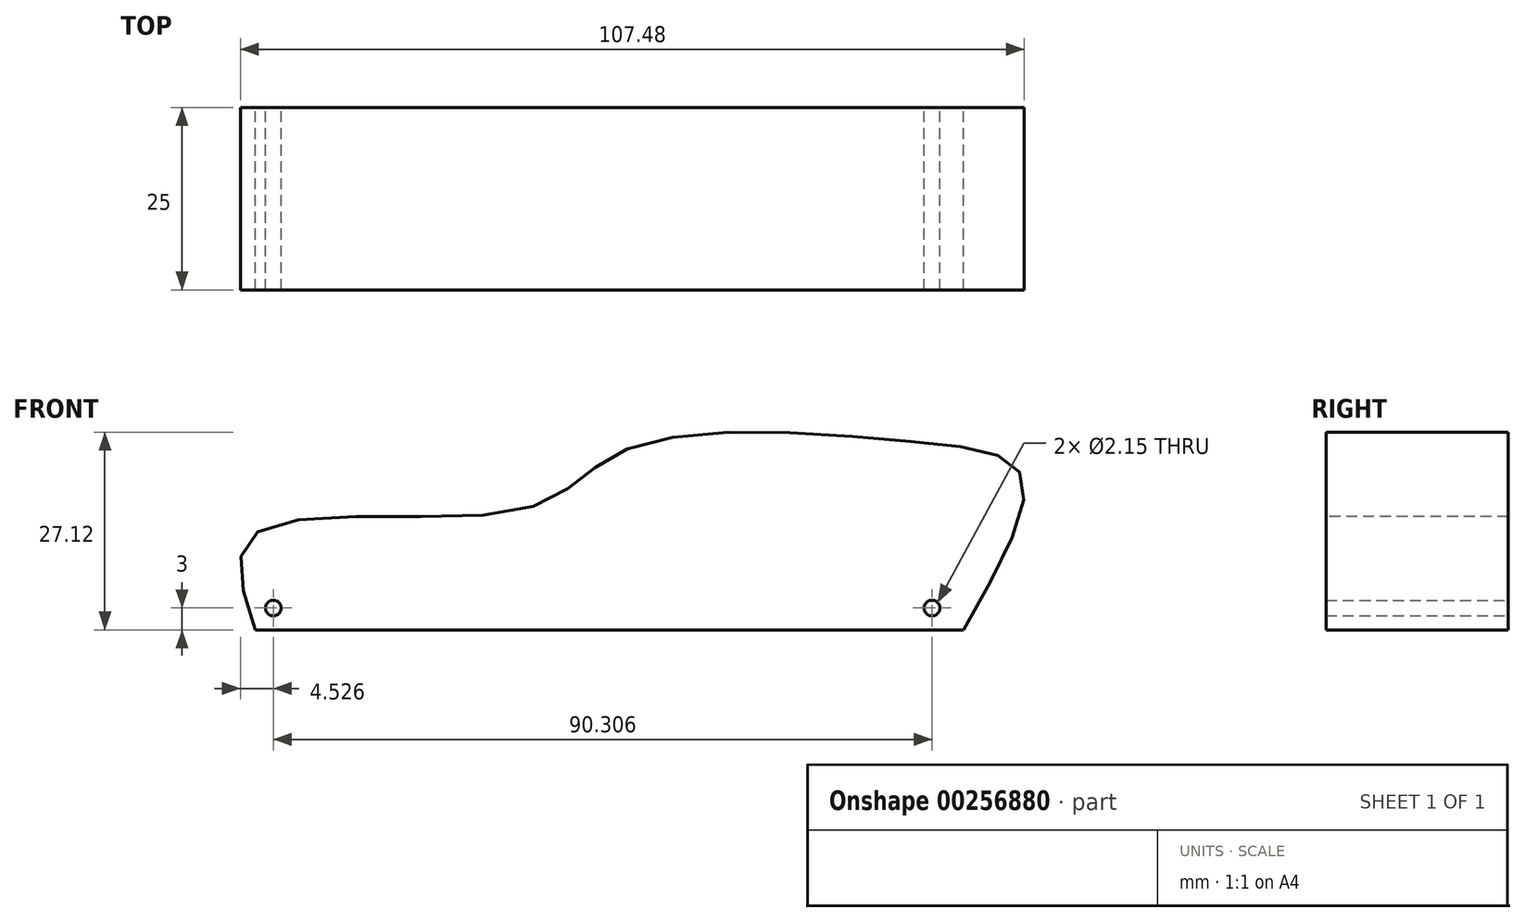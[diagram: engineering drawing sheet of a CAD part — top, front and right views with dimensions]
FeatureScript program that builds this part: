
annotation { "Feature Type Name" : "Feature", "Feature Type Description" : "" }
export const myFeature = defineFeature(function(context is Context, id is Id, definition is map)
    precondition{}
    {
        {
            var Q0;
            Q0=qCreatedBy(makeId("Front.planeOp"),FACE);
            var sketch = newSketch(context, id + "F0", { "sketchPlane" : qUnion([Q0])});
            skLineSegment(sketch, "E0", {"start": v(-46.22, 0) * mm, "end": v(0, 0) * mm});
            skLineSegment(sketch, "E1", {"start": v(0, 0) * mm, "end": v(50.9, 0) * mm});
            skFitSpline(sketch, "E2", {"points": [v(-46.22, 0) * mm, v(-46.22, 13.24) * mm, v(-9.51, 16.55) * mm, v(5.06, 24.94) * mm, v(43.9, 25.82) * mm, v(58.91, 20.97) * mm, v(50.9, 0) * mm], "startDerivative": vector(-42, 126.6) * mm, "endDerivative": vector(-87.27, -152.55) * mm});
            skLineSegment(sketch, "E3", {"start": v(-42.18, 0) * mm, "end": v(-42.18, 4.4) * mm});
            skSolve(sketch);
        }
        {
            var Q0;
            Q0=makeQuery(id+"F0.imprint","IMPRINT",FACE,{"disambiguationData":[TD([[makeQuery(id+"F0.imprint","IMPRINT",EDGE,{"derivedFrom":sQuery(id+"F0.wireOp",EDGE,"E0")}),1.0]])]});
            extrude(context, id + "F1", {"entities" : qUnion([Q0]), "depth" : 25 * mm});
        }
        {
            var Q0;
            Q0=makeQuery(id+"F1.opExtrude","CAP_FACE",FACE,{"disambiguationData":[OSD([sQuery(id+"F0.wireOp",EDGE,"E0"),sQuery(id+"F0.wireOp",EDGE,"E1"),sQuery(id+"F0.wireOp",EDGE,"E2")])],"isStart":false});
            var sketch = newSketch(context, id + "F2", { "sketchPlane" : qUnion([Q0])});
            skSolve(sketch);
        }
        {
            var Q0;
            Q0=makeQuery(id+"F1.opExtrude","CAP_FACE",FACE,{"disambiguationData":[OSD([sQuery(id+"F0.wireOp",EDGE,"E0"),sQuery(id+"F0.wireOp",EDGE,"E1"),sQuery(id+"F0.wireOp",EDGE,"E2")])],"isStart":true});
            var sketch = newSketch(context, id + "F3", { "sketchPlane" : qUnion([Q0])});
            skLineSegment(sketch, "E4", {"start": v(43.74, 3) * mm, "end": v(43.74, 0) * mm});
            skCircle(sketch, "E5", {"center": v(43.74, 3) * mm, "radius": 1.07 * mm});
            skLineSegment(sketch, "E6", {"start": v(-46.56, 0) * mm, "end": v(-46.56, 3) * mm});
            skCircle(sketch, "E7", {"center": v(-46.56, 3) * mm, "radius": 1.07 * mm});
            skSolve(sketch);
        }
        {
            var Q0;
            Q0=makeQuery(id+"F3.imprint","IMPRINT",FACE,{"disambiguationData":[TD([[makeQuery(id+"F3.imprint","IMPRINT",EDGE,{"derivedFrom":sQuery(id+"F3.wireOp",EDGE,"E7")}),1.0]])]});
            extrude(context, id + "F4", {"entities" : qUnion([Q0]), "operationType" : NewBodyOperationType.REMOVE, "endBound" : BoundingType.THROUGH_ALL, "oppositeDirection" : true, "depth" : 25 * mm});
        }
        {
            var Q0;
            Q0=makeQuery(id+"F3.imprint","IMPRINT",FACE,{"disambiguationData":[TD([[makeQuery(id+"F3.imprint","IMPRINT",EDGE,{"derivedFrom":sQuery(id+"F3.wireOp",EDGE,"E5")}),1.0]])]});
            extrude(context, id + "F5", {"entities" : qUnion([Q0]), "operationType" : NewBodyOperationType.REMOVE, "endBound" : BoundingType.THROUGH_ALL, "oppositeDirection" : true, "depth" : 25 * mm});
        }
    });
